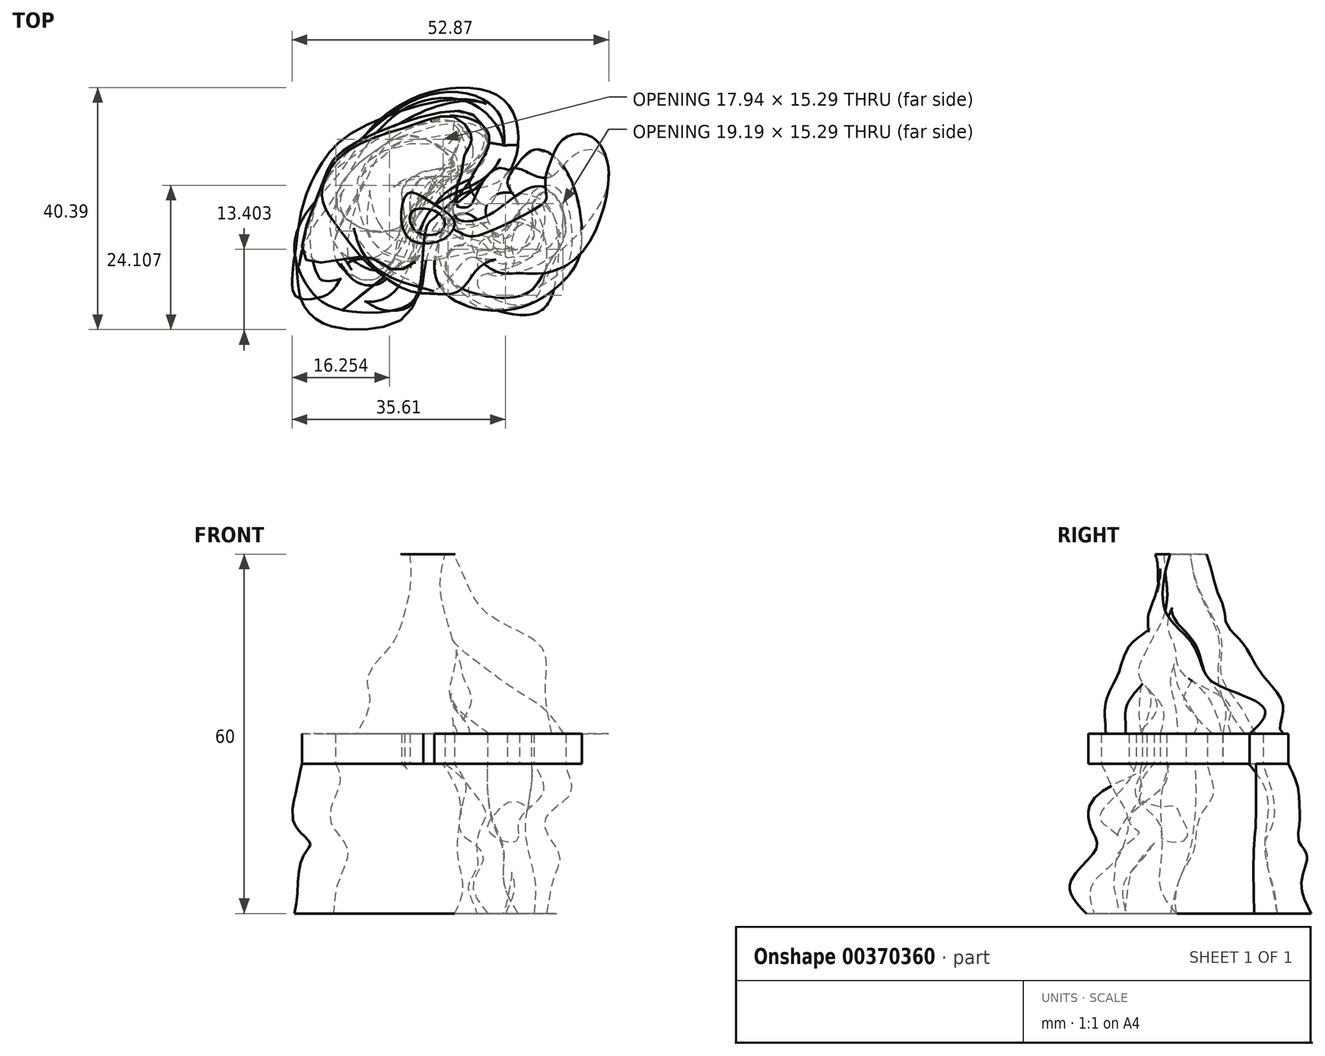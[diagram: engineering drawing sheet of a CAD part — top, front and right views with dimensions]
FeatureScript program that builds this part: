
annotation { "Feature Type Name" : "Feature", "Feature Type Description" : "" }
export const myFeature = defineFeature(function(context is Context, id is Id, definition is map)
    precondition{}
    {
        {
            var Q0;
            Q0=qCreatedBy(makeId("Top.planeOp"),FACE);
            cPlane(context, id + "F0", {"entities" : qUnion([Q0]), "cplaneType" : CPlaneType.OFFSET, "offset" : 5 * mm, "width" : 152.4 * mm, "height" : 152.4 * mm});
        }
        {
            var Q0;
            Q0=qCreatedBy(id+"F0.planeOp",FACE);
            var sketch = newSketch(context, id + "F1", { "sketchPlane" : qUnion([Q0])});
            skFitSpline(sketch, "E0", {"points": [v(10.66, 15.7) * mm, v(7.94, 23.44) * mm, v(-3.49, 24.6) * mm, v(-13.56, 18.8) * mm, v(-19.18, 11.04) * mm, v(-24.6, 4.46) * mm, v(-26.73, -1.55) * mm, v(-25, -7.17) * mm, v(-20.34, -11.43) * mm, v(-8.91, -11.62) * mm, v(-5.81, -7.94) * mm, v(-4.65, 1.94) * mm, v(-3.1, 3.68) * mm, v(1.55, 7.56) * mm, v(7.56, 9.69) * mm, v(10.66, 15.7) * mm]});
            skSolve(sketch);
        }
        {
            var Q0;
            Q0=qCreatedBy(id+"F0.planeOp",FACE);
            var sketch = newSketch(context, id + "F2", { "sketchPlane" : qUnion([Q0])});
            skFitSpline(sketch, "E1", {"points": [v(0, 2.71) * mm, v(-2.71, -1.94) * mm, v(1.74, -9.3) * mm, v(12.98, -12.6) * mm, v(16.66, -8.33) * mm, v(16.66, 3.68) * mm, v(13.95, 6.78) * mm, v(10.85, 7.56) * mm, v(6.97, 7.36) * mm, v(5.23, 4.84) * mm, v(6, 1.94) * mm, v(6.4, -1.74) * mm, v(4.84, -2.71) * mm, v(3.68, -2.71) * mm, v(2.9, 0) * mm, v(3.1, 2.71) * mm, v(0, 2.71) * mm]});
            skSolve(sketch);
        }
        {
            var Q0;
            Q0=qCreatedBy(id+"F0.planeOp",FACE);
            var sketch = newSketch(context, id + "F3", { "sketchPlane" : qUnion([Q0])});
            skFitSpline(sketch, "E2", {"points": [v(0, 19.57) * mm, v(-10.46, 16.66) * mm, v(-15.7, 7.94) * mm, v(-20.15, -2.32) * mm, v(-15.5, -6.78) * mm, v(-11.82, -5.81) * mm, v(-8.72, 0) * mm, v(-4.26, 8.14) * mm, v(2.13, 11.62) * mm, v(5.62, 17.05) * mm, v(0, 19.57) * mm]});
            skSolve(sketch);
        }
        {
            var Q0;
            Q0=qCreatedBy(id+"F0.planeOp",FACE);
            var sketch = newSketch(context, id + "F4", { "sketchPlane" : qUnion([Q0])});
            skFitSpline(sketch, "E3", {"points": [v(13.37, 1.74) * mm, v(9.5, 2.71) * mm, v(8.14, 0) * mm, v(8.33, -5.23) * mm, v(4.84, -6) * mm, v(3.87, -7.75) * mm, v(8.33, -10.66) * mm, v(12.98, -10.46) * mm, v(15.11, -6) * mm, v(15.11, 0) * mm, v(13.37, 1.74) * mm]});
            skSolve(sketch);
        }
        {
            var Q0;
            Q0=qCreatedBy(id+"F0.planeOp",FACE);
            cPlane(context, id + "F5", {"entities" : qUnion([Q0]), "cplaneType" : CPlaneType.OFFSET, "offset" : 5 * mm, "width" : 152.4 * mm, "height" : 152.4 * mm});
        }
        {
            var Q0;
            Q0=qCreatedBy(id+"F5.planeOp",FACE);
            var sketch = newSketch(context, id + "F6", { "sketchPlane" : qUnion([Q0])});
            skFitSpline(sketch, "E4", {"points": [v(3.1, 22.47) * mm, v(-6.78, 22.47) * mm, v(-14.14, 16.27) * mm, v(-20.15, 6.97) * mm, v(-24.6, 0) * mm, v(-25.96, -8.72) * mm, v(-21.31, -14.34) * mm, v(-8.91, -13.17) * mm, v(-6.78, -6.2) * mm, v(-4.07, 4.46) * mm, v(3.68, 9.3) * mm, v(8.33, 15.3) * mm, v(3.1, 22.47) * mm]});
            skSolve(sketch);
        }
        {
            var Q0;
            Q0=qCreatedBy(id+"F5.planeOp",FACE);
            var sketch = newSketch(context, id + "F7", { "sketchPlane" : qUnion([Q0])});
            skFitSpline(sketch, "E5", {"points": [v(1.74, 0) * mm, v(4.65, -1.74) * mm, v(8.91, 1.94) * mm, v(8.72, 9.3) * mm, v(12.6, 10.85) * mm, v(18.6, 9.5) * mm, v(20.54, 4.84) * mm, v(19.37, 0) * mm, v(16.47, -7.36) * mm, v(13.95, -9.88) * mm, v(6.4, -13.17) * mm, v(2.9, -12.6) * mm, v(0, -11.04) * mm, v(-1.94, -4.65) * mm, v(0, -1.74) * mm, v(1.74, 0) * mm]});
            skSolve(sketch);
        }
        {
            var Q0;
            Q0=qCreatedBy(id+"F5.planeOp",FACE);
            var sketch = newSketch(context, id + "F8", { "sketchPlane" : qUnion([Q0])});
            skFitSpline(sketch, "E6", {"points": [v(-1.95, 18.75) * mm, v(-12.28, 15.24) * mm, v(-14.78, 10.42) * mm, v(-18.5, 3.1) * mm, v(-19.3, -2.81) * mm, v(-16.29, -7.23) * mm, v(-12.38, -7.43) * mm, v(-10.17, -4.72) * mm, v(-8.97, 1.8) * mm, v(-4.46, 7.41) * mm, v(2.56, 12.43) * mm, v(2.56, 16.84) * mm, v(-1.95, 18.75) * mm]});
            skSolve(sketch);
        }
        {
            var Q0;
            Q0=qCreatedBy(id+"F5.planeOp",FACE);
            var sketch = newSketch(context, id + "F9", { "sketchPlane" : qUnion([Q0])});
            skFitSpline(sketch, "E7", {"points": [v(13.5, 3) * mm, v(10.59, 2) * mm, v(9.38, -0.9) * mm, v(9.99, -4.12) * mm, v(6.88, -6.02) * mm, v(4.47, -5.32) * mm, v(2.87, -5.82) * mm, v(2.46, -7.73) * mm, v(3.17, -10.84) * mm, v(9.58, -10.23) * mm, v(15.71, -5.86) * mm, v(15.71, 1.14) * mm, v(13.5, 3) * mm]});
            skSolve(sketch);
        }
        {
            var Q0;
            Q0=qCreatedBy(id+"F5.planeOp",FACE);
            cPlane(context, id + "F10", {"entities" : qUnion([Q0]), "cplaneType" : CPlaneType.OFFSET, "offset" : 5 * mm, "width" : 152.4 * mm, "height" : 152.4 * mm});
        }
        {
            var Q0;
            Q0=qCreatedBy(id+"F10.planeOp",FACE);
            var sketch = newSketch(context, id + "F11", { "sketchPlane" : qUnion([Q0])});
            skFitSpline(sketch, "E8", {"points": [v(-8.91, 21.9) * mm, v(2.9, 24.02) * mm, v(7.75, 19.95) * mm, v(7.17, 12.6) * mm, v(0, 5.62) * mm, v(-3.1, 2.32) * mm, v(-6.97, -3.49) * mm, v(-10.46, -9.5) * mm, v(-18.21, -11.04) * mm, v(-24.4, -7.17) * mm, v(-24.02, 2.9) * mm, v(-21.9, 8.91) * mm, v(-19.57, 12.2) * mm, v(-8.91, 21.9) * mm]});
            skSolve(sketch);
        }
        {
            var Q0;
            Q0=qCreatedBy(id+"F10.planeOp",FACE);
            var sketch = newSketch(context, id + "F12", { "sketchPlane" : qUnion([Q0])});
            skFitSpline(sketch, "E9", {"points": [v(0, -2.13) * mm, v(1.74, 2.13) * mm, v(3.87, 2.52) * mm, v(7.36, 2.13) * mm, v(9.88, 5.81) * mm, v(12.98, 7.56) * mm, v(16.85, 6.97) * mm, v(18.21, 3.1) * mm, v(18.4, -1.55) * mm, v(16.27, -4.84) * mm, v(12.2, -6.97) * mm, v(8.91, -7.75) * mm, v(4.26, -8.14) * mm, v(1.55, -5.62) * mm, v(0, -2.13) * mm]});
            skSolve(sketch);
        }
        {
            var Q0;
            Q0=qCreatedBy(id+"F10.planeOp",FACE);
            var sketch = newSketch(context, id + "F13", { "sketchPlane" : qUnion([Q0])});
            skFitSpline(sketch, "E10", {"points": [v(14.7, 5.4) * mm, v(11.29, 4) * mm, v(10.09, 2.3) * mm, v(6.68, -2.41) * mm, v(4.17, -2.31) * mm, v(3.87, -4.02) * mm, v(6.07, -6.32) * mm, v(13.6, -5.72) * mm, v(16.9, -2.41) * mm, v(17.4, 1.7) * mm, v(14.7, 5.4) * mm]});
            skSolve(sketch);
        }
        {
            var Q0;
            Q0=qCreatedBy(id+"F10.planeOp",FACE);
            var sketch = newSketch(context, id + "F14", { "sketchPlane" : qUnion([Q0])});
            skFitSpline(sketch, "E11", {"points": [v(-0.95, 17.44) * mm, v(-13.38, 14.13) * mm, v(-15.29, 9.52) * mm, v(-17.8, -1.1) * mm, v(-15.49, -6.93) * mm, v(-8.77, -3.01) * mm, v(-5.46, 7.72) * mm, v(0, 11.53) * mm, v(3.87, 13.93) * mm, v(4.57, 17.24) * mm, v(-0.95, 17.44) * mm]});
            skSolve(sketch);
        }
        {
            var Q0;
            Q0=qCreatedBy(id+"F10.planeOp",FACE);
            cPlane(context, id + "F15", {"entities" : qUnion([Q0]), "cplaneType" : CPlaneType.OFFSET, "offset" : 5 * mm, "width" : 152.4 * mm, "height" : 152.4 * mm});
        }
        {
            var Q0;
            Q0=qCreatedBy(id+"F15.planeOp",FACE);
            var sketch = newSketch(context, id + "F16", { "sketchPlane" : qUnion([Q0])});
            skFitSpline(sketch, "E12", {"points": [v(-17.05, 13.75) * mm, v(-5.81, 21.31) * mm, v(5.62, 21.9) * mm, v(4.84, 11.82) * mm, v(0, 8.72) * mm, v(-4.65, 3.68) * mm, v(-7.17, -3.87) * mm, v(-8.14, -10.07) * mm, v(-10.07, -11.62) * mm, v(-13.17, -11.43) * mm, v(-15.3, -8.91) * mm, v(-15.89, -6.78) * mm, v(-18.6, -6.4) * mm, v(-20.54, -8.52) * mm, v(-22.09, -9.3) * mm, v(-25.18, -9.5) * mm, v(-26.54, -8.72) * mm, v(-26.35, -2.71) * mm, v(-24.22, 7.36) * mm, v(-17.05, 13.75) * mm]});
            skSolve(sketch);
        }
        {
            var Q0;
            Q0=qCreatedBy(id+"F15.planeOp",FACE);
            var sketch = newSketch(context, id + "F17", { "sketchPlane" : qUnion([Q0])});
            skFitSpline(sketch, "E13", {"points": [v(0, 18.6) * mm, v(-12.7, 13.89) * mm, v(-15.9, 9.73) * mm, v(-20.33, 2.38) * mm, v(-19.78, -1.22) * mm, v(-16.31, -4) * mm, v(-11.74, -4.68) * mm, v(-4.67, 7.23) * mm, v(0, 14.02) * mm, v(0, 18.6) * mm]});
            skSolve(sketch);
        }
        {
            var Q0;
            Q0=qCreatedBy(id+"F15.planeOp",FACE);
            var sketch = newSketch(context, id + "F18", { "sketchPlane" : qUnion([Q0])});
            skFitSpline(sketch, "E14", {"points": [v(14.6, 5.85) * mm, v(11.4, 5.3) * mm, v(9.32, 1.83) * mm, v(5.72, 0) * mm, v(4.75, -3.02) * mm, v(6.7, -5.24) * mm, v(11.54, -3.85) * mm, v(13.9, -1.5) * mm, v(14.6, 5.85) * mm]});
            skSolve(sketch);
        }
        {
            var Q0;
            Q0=qCreatedBy(id+"F15.planeOp",FACE);
            cPlane(context, id + "F19", {"entities" : qUnion([Q0]), "cplaneType" : CPlaneType.OFFSET, "offset" : 5 * mm, "width" : 152.4 * mm, "height" : 152.4 * mm});
        }
        {
            var Q0;
            Q0=qCreatedBy(id+"F19.planeOp",FACE);
            var sketch = newSketch(context, id + "F20", { "sketchPlane" : qUnion([Q0])});
            skFitSpline(sketch, "E15", {"points": [v(0, -2.9) * mm, v(2.13, 2.32) * mm, v(6.97, -1.74) * mm, v(10.27, -2.71) * mm, v(13.17, 2.32) * mm, v(11.62, 3.49) * mm, v(8.78, 5.55) * mm, v(7.73, 7.13) * mm, v(10.2, 11.79) * mm, v(15.4, 12.24) * mm, v(18.99, 10.07) * mm, v(21.31, 3.87) * mm, v(21.5, -4.26) * mm, v(17.24, -7.75) * mm, v(10.46, -8.72) * mm, v(3.68, -8.72) * mm, v(0, -7.56) * mm, v(0, -2.9) * mm]});
            skSolve(sketch);
        }
        {
            var Q0;
            Q0=qCreatedBy(id+"F19.planeOp",FACE);
            var sketch = newSketch(context, id + "F21", { "sketchPlane" : qUnion([Q0])});
            skFitSpline(sketch, "E16", {"points": [v(-25.96, -5.81) * mm, v(-22.09, -6.97) * mm, v(-18.6, -4.84) * mm, v(-16.47, -3.3) * mm, v(-13.37, -3.87) * mm, v(-12.79, -6.4) * mm, v(-11.82, -9.3) * mm, v(-7.56, -10.07) * mm, v(-5.42, -7.94) * mm, v(-4.65, -3.3) * mm, v(0, 6) * mm, v(1.55, 8.33) * mm, v(5.62, 15.89) * mm, v(2.32, 22.28) * mm, v(-4.26, 22.67) * mm, v(-15.5, 18.21) * mm, v(-22.09, 12.79) * mm, v(-25.57, 2.71) * mm, v(-25.96, -5.81) * mm]});
            skSolve(sketch);
        }
        {
            var Q0;
            Q0=qCreatedBy(id+"F19.planeOp",FACE);
            var sketch = newSketch(context, id + "F22", { "sketchPlane" : qUnion([Q0])});
            skFitSpline(sketch, "E17", {"points": [v(0, 18.32) * mm, v(-8.7, 16.52) * mm, v(-12.3, 13.47) * mm, v(-17.28, 9.87) * mm, v(-19.5, 3.08) * mm, v(-14.37, 0) * mm, v(-8.7, 0) * mm, v(-3.15, 9.17) * mm, v(1.56, 13.05) * mm, v(0, 18.32) * mm]});
            skSolve(sketch);
        }
        {
            var Q0;
            Q0=qCreatedBy(id+"F19.planeOp",FACE);
            var sketch = newSketch(context, id + "F23", { "sketchPlane" : qUnion([Q0])});
            skFitSpline(sketch, "E18", {"points": [v(12.65, 7.1) * mm, v(13.9, 3.9) * mm, v(14.73, 0) * mm, v(13.2, -2.6) * mm, v(7.8, -4.13) * mm, v(5.44, -3.44) * mm, v(3.78, -4.13) * mm, v(3.92, -6.62) * mm, v(16.8, -5.52) * mm, v(19.44, 0) * mm, v(16.4, 8.76) * mm, v(12.65, 7.1) * mm]});
            skSolve(sketch);
        }
        {
            var Q0;
            Q0=qCreatedBy(id+"F19.planeOp",FACE);
            cPlane(context, id + "F24", {"entities" : qUnion([Q0]), "cplaneType" : CPlaneType.OFFSET, "offset" : 5 * mm, "width" : 152.4 * mm, "height" : 152.4 * mm});
        }
        {
            var Q0;
            Q0=qCreatedBy(id+"F24.planeOp",FACE);
            var sketch = newSketch(context, id + "F25", { "sketchPlane" : qUnion([Q0])});
            skFitSpline(sketch, "E19", {"points": [v(-25, -3.3) * mm, v(-16.66, -3.1) * mm, v(-12.79, -3.68) * mm, v(-9.5, -5.23) * mm, v(-5.62, -2.71) * mm, v(-5.42, 0) * mm, v(-6.97, 3.3) * mm, v(-7.36, 6.78) * mm, v(-6, 9.69) * mm, v(-3.68, 10.46) * mm, v(0, 10.46) * mm, v(5.04, 13.17) * mm, v(4.07, 19.95) * mm, v(-2.32, 21.12) * mm, v(-15.3, 16.66) * mm, v(-20.34, 12.98) * mm, v(-22.67, 7.56) * mm, v(-25, -3.3) * mm]});
            skSolve(sketch);
        }
        {
            var Q0;
            Q0=qCreatedBy(id+"F24.planeOp",FACE);
            var sketch = newSketch(context, id + "F26", { "sketchPlane" : qUnion([Q0])});
            skFitSpline(sketch, "E20", {"points": [v(2.9, 3.87) * mm, v(0, 3.87) * mm, v(-2.09, 1.21) * mm, v(-3.3, -5.42) * mm, v(0, -10.27) * mm, v(10.46, -11.62) * mm, v(19.18, -6) * mm, v(21.31, 0) * mm, v(18.4, 11.82) * mm, v(13.56, 14.92) * mm, v(10.66, 12.61) * mm, v(8.86, 9.23) * mm, v(10.46, 6.4) * mm, v(10.46, 2.13) * mm, v(8.14, 0) * mm, v(2.9, 3.87) * mm]});
            skSolve(sketch);
        }
        {
            var Q0;
            Q0=qCreatedBy(id+"F24.planeOp",FACE);
            var sketch = newSketch(context, id + "F27", { "sketchPlane" : qUnion([Q0])});
            skFitSpline(sketch, "E21", {"points": [v(-6.2, 17.07) * mm, v(-12.7, 15) * mm, v(-17.56, 10.98) * mm, v(-19.64, 5.3) * mm, v(-14.1, 1.28) * mm, v(-11.18, 1.28) * mm, v(-8.41, 2.8) * mm, v(-8.7, 8.2) * mm, v(-3.84, 11.53) * mm, v(0, 12.36) * mm, v(-6.2, 17.07) * mm]});
            skSolve(sketch);
        }
        {
            var Q0;
            Q0=qCreatedBy(id+"F24.planeOp",FACE);
            var sketch = newSketch(context, id + "F28", { "sketchPlane" : qUnion([Q0])});
            skFitSpline(sketch, "E22", {"points": [v(15.98, 7.79) * mm, v(12.93, 5.57) * mm, v(13.2, 0) * mm, v(10.02, -1.91) * mm, v(5.72, -2.05) * mm, v(0, -1.22) * mm, v(-1.48, -5.24) * mm, v(2.12, -8.7) * mm, v(12.1, -9.12) * mm, v(15.84, -4) * mm, v(18.6, 1.28) * mm, v(15.98, 7.79) * mm]});
            skSolve(sketch);
        }
        {
            var Q0;
            Q0=qCreatedBy(id+"F24.planeOp",FACE);
            cPlane(context, id + "F29", {"entities" : qUnion([Q0]), "cplaneType" : CPlaneType.OFFSET, "offset" : 5 * mm, "width" : 152.4 * mm, "height" : 152.4 * mm});
        }
        {
            var Q0;
            Q0=qCreatedBy(id+"F29.planeOp",FACE);
            var sketch = newSketch(context, id + "F30", { "sketchPlane" : qUnion([Q0])});
            skFitSpline(sketch, "E23", {"points": [v(16.27, 10.46) * mm, v(20.54, 14.34) * mm, v(24.8, 14.14) * mm, v(25.57, 8.91) * mm, v(23.44, 4.46) * mm, v(17.24, -2.32) * mm, v(7.36, -5.62) * mm, v(3.1, -3.1) * mm, v(0, -5.62) * mm, v(-5.23, -9.1) * mm, v(-14.14, -4.46) * mm, v(-18.02, 0) * mm, v(-21.31, 4.65) * mm, v(-22.09, 7.94) * mm, v(-18.02, 14.53) * mm, v(-3.49, 19.76) * mm, v(0, 20.54) * mm, v(5.23, 18.4) * mm, v(5.04, 13.95) * mm, v(2.52, 9.3) * mm, v(5.42, 5.62) * mm, v(8.14, 9.88) * mm, v(9.88, 11.82) * mm, v(13.17, 10.66) * mm, v(16.27, 10.46) * mm]});
            skSolve(sketch);
        }
        {
            var Q0;
            Q0=qCreatedBy(id+"F29.planeOp",FACE);
            var sketch = newSketch(context, id + "F31", { "sketchPlane" : qUnion([Q0])});
            skFitSpline(sketch, "E24", {"points": [v(0, 14.16) * mm, v(-13.54, 13.75) * mm, v(-16.17, 6.13) * mm, v(-11.46, -2.74) * mm, v(-1.48, -2.6) * mm, v(3.78, 0) * mm, v(7.1, -2.74) * mm, v(17.36, 0) * mm, v(16.95, 7.1) * mm, v(12.93, 8.62) * mm, v(5.03, 3.63) * mm, v(0, 4.05) * mm, v(0, 14.16) * mm]});
            skSolve(sketch);
        }
        {
            var Q0;
            Q0=qCreatedBy(id+"F29.planeOp",FACE);
            cPlane(context, id + "F32", {"entities" : qUnion([Q0]), "cplaneType" : CPlaneType.OFFSET, "offset" : 5 * mm, "width" : 152.4 * mm, "height" : 152.4 * mm});
        }
        {
            var Q0;
            Q0=qCreatedBy(id+"F32.planeOp",FACE);
            var sketch = newSketch(context, id + "F33", { "sketchPlane" : qUnion([Q0])});
            skFitSpline(sketch, "E25", {"points": [v(-6.97, 17.82) * mm, v(-15.89, 14.34) * mm, v(-18.4, 7.36) * mm, v(-17.63, 0) * mm, v(-10.66, -5.42) * mm, v(-10.07, -5.62) * mm, v(-1.94, -9.1) * mm, v(1.94, -7.56) * mm, v(4.26, -4.65) * mm, v(8.14, -3.49) * mm, v(13.37, -5.42) * mm, v(19.76, -3.3) * mm, v(23.44, 2.9) * mm, v(24.4, 10.07) * mm, v(21.7, 16.08) * mm, v(18.02, 16.08) * mm, v(15.7, 11.82) * mm, v(14.14, 8.91) * mm, v(11.82, 8.72) * mm, v(10.07, 9.69) * mm, v(6.78, 11.43) * mm, v(3.68, 6.78) * mm, v(3.3, 5.04) * mm, v(0, 4.26) * mm, v(0, 7.56) * mm, v(0, 14.53) * mm, v(2.71, 16.66) * mm, v(0, 20.34) * mm, v(-6.97, 17.82) * mm]});
            skSolve(sketch);
        }
        {
            var Q0;
            Q0=qCreatedBy(id+"F32.planeOp",FACE);
            var sketch = newSketch(context, id + "F34", { "sketchPlane" : qUnion([Q0])});
            skFitSpline(sketch, "E26", {"points": [v(-2.18, 10.14) * mm, v(-12.3, 12.64) * mm, v(-14.1, 7.51) * mm, v(-10.08, 0) * mm, v(3.92, 0) * mm, v(11.13, -1.36) * mm, v(13.76, 3.9) * mm, v(10.16, 4.46) * mm, v(4.9, 2.94) * mm, v(0, 3.08) * mm, v(-2.18, 10.14) * mm]});
            skSolve(sketch);
        }
        {
            var Q0;
            Q0=qCreatedBy(id+"F32.planeOp",FACE);
            cPlane(context, id + "F35", {"entities" : qUnion([Q0]), "cplaneType" : CPlaneType.OFFSET, "offset" : 5 * mm, "width" : 152.4 * mm, "height" : 152.4 * mm});
        }
        {
            var Q0;
            Q0=qCreatedBy(id+"F35.planeOp",FACE);
            var sketch = newSketch(context, id + "F36", { "sketchPlane" : qUnion([Q0])});
            skFitSpline(sketch, "E27", {"points": [v(-15.11, 12.79) * mm, v(-10.27, 15.11) * mm, v(-2.32, 16.66) * mm, v(0, 16.66) * mm, v(1.36, 12.01) * mm, v(0, 8.33) * mm, v(0, 5.81) * mm, v(1.74, 5.04) * mm, v(4.84, 3.87) * mm, v(10.07, 4.84) * mm, v(13.75, 7.36) * mm, v(18.8, 6) * mm, v(18.21, 0) * mm, v(14.72, -2.32) * mm, v(8.72, -2.52) * mm, v(6.2, -1.94) * mm, v(2.32, -3.1) * mm, v(0, -5.42) * mm, v(-8.91, -6.78) * mm, v(-16.27, 0) * mm, v(-15.11, 12.79) * mm]});
            skSolve(sketch);
        }
        {
            var Q0;
            Q0=qCreatedBy(id+"F35.planeOp",FACE);
            var sketch = newSketch(context, id + "F37", { "sketchPlane" : qUnion([Q0])});
            skFitSpline(sketch, "E28", {"points": [v(-4.4, 10) * mm, v(-12.3, 7.51) * mm, v(-13.82, 0) * mm, v(-8.27, -3.16) * mm, v(-1.48, -3.16) * mm, v(3.92, 0) * mm, v(6.41, 1.28) * mm, v(4.9, 2.52) * mm, v(0, 1.97) * mm, v(-2.32, 7.23) * mm, v(-4.4, 10) * mm]});
            skSolve(sketch);
        }
        {
            var Q0;
            Q0=qCreatedBy(id+"F35.planeOp",FACE);
            cPlane(context, id + "F38", {"entities" : qUnion([Q0]), "cplaneType" : CPlaneType.OFFSET, "offset" : 5 * mm, "width" : 152.4 * mm, "height" : 152.4 * mm});
        }
        {
            var Q0;
            Q0=qCreatedBy(id+"F38.planeOp",FACE);
            var sketch = newSketch(context, id + "F39", { "sketchPlane" : qUnion([Q0])});
            skFitSpline(sketch, "E29", {"points": [v(-3.49, 13.56) * mm, v(-12.01, 11.82) * mm, v(-12.98, 5.81) * mm, v(-9.1, -2.52) * mm, v(-4.26, -4.84) * mm, v(0, -2.52) * mm, v(10.07, -1.74) * mm, v(16.47, 1.74) * mm, v(12.79, 5.81) * mm, v(6.4, 2.71) * mm, v(1.36, 3.3) * mm, v(0, 9.1) * mm, v(-3.49, 13.56) * mm]});
            skSolve(sketch);
        }
        {
            var Q0;
            Q0=qCreatedBy(id+"F38.planeOp",FACE);
            var sketch = newSketch(context, id + "F40", { "sketchPlane" : qUnion([Q0])});
            skFitSpline(sketch, "E30", {"points": [v(-1.76, 8.76) * mm, v(-8.55, 9.73) * mm, v(-10.21, 4.32) * mm, v(-5.36, -1.64) * mm, v(0, 0) * mm, v(0, 2.25) * mm, v(-1.76, 8.76) * mm]});
            skSolve(sketch);
        }
        {
            var Q0;
            Q0=qCreatedBy(id+"F38.planeOp",FACE);
            cPlane(context, id + "F41", {"entities" : qUnion([Q0]), "cplaneType" : CPlaneType.OFFSET, "offset" : 5 * mm, "width" : 152.4 * mm, "height" : 152.4 * mm});
        }
        {
            var Q0;
            Q0=qCreatedBy(id+"F41.planeOp",FACE);
            var sketch = newSketch(context, id + "F42", { "sketchPlane" : qUnion([Q0])});
            skFitSpline(sketch, "E31", {"points": [v(-2.32, 9.5) * mm, v(-9.88, 10.07) * mm, v(-10.07, 3.49) * mm, v(-6.78, 0) * mm, v(0, -1.94) * mm, v(5.62, 0) * mm, v(4.46, 1.94) * mm, v(0, 1.55) * mm, v(0, 2.13) * mm, v(0, 6.2) * mm, v(-2.32, 9.5) * mm]});
            skSolve(sketch);
        }
        {
            var Q0;
            Q0=qCreatedBy(id+"F41.planeOp",FACE);
            var sketch = newSketch(context, id + "F43", { "sketchPlane" : qUnion([Q0])});
            skFitSpline(sketch, "E32", {"points": [v(-3.14, 7.61) * mm, v(-7.34, 7.94) * mm, v(-8.33, 4.32) * mm, v(-7.1, 2.17) * mm, v(-3.22, 0.7) * mm, v(-1.66, 2.26) * mm, v(-3.14, 7.61) * mm]});
            skSolve(sketch);
        }
        {
            var Q0;
            Q0=qCreatedBy(id+"F41.planeOp",FACE);
            cPlane(context, id + "F44", {"entities" : qUnion([Q0]), "cplaneType" : CPlaneType.OFFSET, "offset" : 5 * mm, "width" : 152.4 * mm, "height" : 152.4 * mm});
        }
        {
            var Q0;
            Q0=qCreatedBy(id+"F44.planeOp",FACE);
            var sketch = newSketch(context, id + "F45", { "sketchPlane" : qUnion([Q0])});
            skFitSpline(sketch, "E33", {"points": [v(-1.74, 5.23) * mm, v(-5.04, 8.72) * mm, v(-9.88, 7.56) * mm, v(-6.2, 0) * mm, v(-2.52, 0) * mm, v(2.13, 0) * mm, v(0, 3.87) * mm, v(-1.74, 5.23) * mm]});
            skSolve(sketch);
        }
        {
            var Q0;
            Q0=qCreatedBy(id+"F44.planeOp",FACE);
            var sketch = newSketch(context, id + "F46", { "sketchPlane" : qUnion([Q0])});
            skFitSpline(sketch, "E34", {"points": [v(-2.81, 4.23) * mm, v(-5.78, 6.13) * mm, v(-7.34, 3.99) * mm, v(-5.28, 1.35) * mm, v(-2.73, 1.51) * mm, v(-2.81, 4.23) * mm]});
            skSolve(sketch);
        }
        {
            var Q0;
            Q0=qCreatedBy(id+"F44.planeOp",FACE);
            cPlane(context, id + "F47", {"entities" : qUnion([Q0]), "cplaneType" : CPlaneType.OFFSET, "offset" : 5 * mm, "width" : 152.4 * mm, "height" : 152.4 * mm});
        }
        {
            var Q0;
            Q0=qCreatedBy(id+"F47.planeOp",FACE);
            var sketch = newSketch(context, id + "F48", { "sketchPlane" : qUnion([Q0])});
            skFitSpline(sketch, "E35", {"points": [v(-3.49, 5.81) * mm, v(-7.36, 7.75) * mm, v(-8.72, 5.62) * mm, v(-7.56, 0) * mm, v(-1.74, 0) * mm, v(0, 2.9) * mm, v(-3.49, 5.81) * mm]});
            skSolve(sketch);
        }
        {
            var Q0;
            Q0=qCreatedBy(id+"F47.planeOp",FACE);
            var sketch = newSketch(context, id + "F49", { "sketchPlane" : qUnion([Q0])});
            skFitSpline(sketch, "E36", {"points": [v(-4.87, 5.06) * mm, v(-7.26, 4.32) * mm, v(-7.18, 2.26) * mm, v(-5.53, 0.77) * mm, v(-2.32, 1.18) * mm, v(-1.74, 3.33) * mm, v(-4.87, 5.06) * mm]});
            skSolve(sketch);
        }
        {
            var Q0;
            Q0=makeQuery(id+"F30.imprint","IMPRINT",FACE,{"disambiguationData":[TD([[makeQuery(id+"F30.imprint","IMPRINT",EDGE,{"derivedFrom":sQuery(id+"F30.wireOp",EDGE,"E23")}),-1.0]])]});
            var Q1;
            Q1=makeQuery(id+"F33.imprint","IMPRINT",FACE,{"disambiguationData":[TD([[makeQuery(id+"F33.imprint","IMPRINT",EDGE,{"derivedFrom":sQuery(id+"F33.wireOp",EDGE,"E25")}),1.0]])]});
            var Q2;
            Q2=makeQuery(id+"F36.imprint","IMPRINT",FACE,{"disambiguationData":[TD([[makeQuery(id+"F36.imprint","IMPRINT",EDGE,{"derivedFrom":sQuery(id+"F36.wireOp",EDGE,"E27")}),-1.0]])]});
            var Q3;
            Q3=makeQuery(id+"F39.imprint","IMPRINT",FACE,{"disambiguationData":[TD([[makeQuery(id+"F39.imprint","IMPRINT",EDGE,{"derivedFrom":sQuery(id+"F39.wireOp",EDGE,"E29")}),1.0]])]});
            var Q4;
            Q4=makeQuery(id+"F42.imprint","IMPRINT",FACE,{"disambiguationData":[TD([[makeQuery(id+"F42.imprint","IMPRINT",EDGE,{"derivedFrom":sQuery(id+"F42.wireOp",EDGE,"E31")}),1.0]])]});
            var Q5;
            Q5=makeQuery(id+"F45.imprint","IMPRINT",FACE,{"disambiguationData":[TD([[makeQuery(id+"F45.imprint","IMPRINT",EDGE,{"derivedFrom":sQuery(id+"F45.wireOp",EDGE,"E33")}),1.0]])]});
            var Q6;
            Q6=makeQuery(id+"F48.imprint","IMPRINT",FACE,{"disambiguationData":[TD([[makeQuery(id+"F48.imprint","IMPRINT",EDGE,{"derivedFrom":sQuery(id+"F48.wireOp",EDGE,"E35")}),1.0]])]});
            loft(context, id + "F50", {"sheetProfilesArray" : [{ "sheetProfileEntities" : qUnion([Q0]) }, { "sheetProfileEntities" : qUnion([Q1]) }, { "sheetProfileEntities" : qUnion([Q2]) }, { "sheetProfileEntities" : qUnion([Q3]) }, { "sheetProfileEntities" : qUnion([Q4]) }, { "sheetProfileEntities" : qUnion([Q5]) }, { "sheetProfileEntities" : qUnion([Q6]) }]});
        }
        {
            var Q1;
            Q1=qSketchRegion(id+"F31",true);
            var Q2;
            Q2=qSketchRegion(id+"F34",true);
            var Q3;
            Q3=qSketchRegion(id+"F37",true);
            var Q4;
            Q4=qSketchRegion(id+"F40",true);
            var Q5;
            Q5=qSketchRegion(id+"F43",true);
            var Q6;
            Q6=qSketchRegion(id+"F46",true);
            var Q7;
            Q7=qSketchRegion(id+"F49",true);
            loft(context, id + "F51", {"operationType" : NewBodyOperationType.REMOVE, "sheetProfilesArray" : [{ "sheetProfileEntities" : qUnion([Q1]) }, { "sheetProfileEntities" : qUnion([Q2]) }, { "sheetProfileEntities" : qUnion([Q3]) }, { "sheetProfileEntities" : qUnion([Q4]) }, { "sheetProfileEntities" : qUnion([Q5]) }, { "sheetProfileEntities" : qUnion([Q6]) }, { "sheetProfileEntities" : qUnion([Q7]) }]});
        }
        {
            var Q0;
            Q0=qSketchRegion(id+"F1",true);
            var Q1;
            Q1=qSketchRegion(id+"F6",true);
            var Q2;
            Q2=qSketchRegion(id+"F11",true);
            var Q3;
            Q3=qSketchRegion(id+"F16",true);
            var Q4;
            Q4=qSketchRegion(id+"F21",true);
            var Q5;
            Q5=qSketchRegion(id+"F25",true);
            loft(context, id + "F52", {"sheetProfilesArray" : [{ "sheetProfileEntities" : qUnion([Q0]) }, { "sheetProfileEntities" : qUnion([Q1]) }, { "sheetProfileEntities" : qUnion([Q2]) }, { "sheetProfileEntities" : qUnion([Q3]) }, { "sheetProfileEntities" : qUnion([Q4]) }, { "sheetProfileEntities" : qUnion([Q5]) }]});
        }
        {
            var Q1;
            Q1=qSketchRegion(id+"F3",true);
            var Q2;
            Q2=qSketchRegion(id+"F8",true);
            var Q3;
            Q3=qSketchRegion(id+"F14",true);
            var Q4;
            Q4=qSketchRegion(id+"F17",true);
            var Q5;
            Q5=qSketchRegion(id+"F22",true);
            var Q6;
            Q6=qSketchRegion(id+"F27",true);
            loft(context, id + "F53", {"operationType" : NewBodyOperationType.REMOVE, "sheetProfilesArray" : [{ "sheetProfileEntities" : qUnion([Q1]) }, { "sheetProfileEntities" : qUnion([Q2]) }, { "sheetProfileEntities" : qUnion([Q3]) }, { "sheetProfileEntities" : qUnion([Q4]) }, { "sheetProfileEntities" : qUnion([Q5]) }, { "sheetProfileEntities" : qUnion([Q6]) }]});
        }
        {
            var Q0;
            Q0=makeQuery(id+"F2.imprint","IMPRINT",FACE,{"disambiguationData":[TD([[makeQuery(id+"F2.imprint","IMPRINT",EDGE,{"derivedFrom":sQuery(id+"F2.wireOp",EDGE,"E1")}),1.0]])]});
            var Q1;
            Q1=makeQuery(id+"F7.imprint","IMPRINT",FACE,{"disambiguationData":[TD([[makeQuery(id+"F7.imprint","IMPRINT",EDGE,{"derivedFrom":sQuery(id+"F7.wireOp",EDGE,"E5")}),-1.0]])]});
            var Q2;
            Q2=makeQuery(id+"F12.imprint","IMPRINT",FACE,{"disambiguationData":[TD([[makeQuery(id+"F12.imprint","IMPRINT",EDGE,{"derivedFrom":sQuery(id+"F12.wireOp",EDGE,"E9")}),-1.0]])]});
            var Q3;
            Q3=makeQuery(id+"F20.imprint","IMPRINT",FACE,{"disambiguationData":[TD([[makeQuery(id+"F20.imprint","IMPRINT",EDGE,{"derivedFrom":sQuery(id+"F20.wireOp",EDGE,"E15")}),-1.0]])]});
            var Q4;
            Q4=makeQuery(id+"F26.imprint","IMPRINT",FACE,{"disambiguationData":[TD([[makeQuery(id+"F26.imprint","IMPRINT",EDGE,{"derivedFrom":sQuery(id+"F26.wireOp",EDGE,"E20")}),1.0]])]});
            loft(context, id + "F54", {"sheetProfilesArray" : [{ "sheetProfileEntities" : qUnion([Q0]) }, { "sheetProfileEntities" : qUnion([Q1]) }, { "sheetProfileEntities" : qUnion([Q2]) }, { "sheetProfileEntities" : qUnion([Q3]) }, { "sheetProfileEntities" : qUnion([Q4]) }]});
        }
        {
            var Q1;
            Q1=qSketchRegion(id+"F4",true);
            var Q2;
            Q2=qSketchRegion(id+"F9",true);
            var Q3;
            Q3=qSketchRegion(id+"F13",true);
            var Q4;
            Q4=qSketchRegion(id+"F18",true);
            var Q5;
            Q5=qSketchRegion(id+"F23",true);
            var Q6;
            Q6=qSketchRegion(id+"F28",true);
            loft(context, id + "F55", {"operationType" : NewBodyOperationType.REMOVE, "sheetProfilesArray" : [{ "sheetProfileEntities" : qUnion([Q1]) }, { "sheetProfileEntities" : qUnion([Q2]) }, { "sheetProfileEntities" : qUnion([Q3]) }, { "sheetProfileEntities" : qUnion([Q4]) }, { "sheetProfileEntities" : qUnion([Q5]) }, { "sheetProfileEntities" : qUnion([Q6]) }]});
        }
        {
            var Q0;
            Q0=makeQuery(id+"F52.opLoft","CAP_FACE",FACE,{"disambiguationData":[OSD([makeQuery(id+"F25.imprint","IMPRINT",FACE,{"disambiguationData":[TD([[makeQuery(id+"F25.imprint","IMPRINT",EDGE,{"derivedFrom":sQuery(id+"F25.wireOp",EDGE,"E19")}),1.0]])]})])],"isStart":true});
            extrude(context, id + "F56", {"entities" : qUnion([Q0]), "depth" : 5 * mm});
        }
        {
            var Q0;
            Q0=makeQuery(id+"F54.opLoft","CAP_FACE",FACE,{"disambiguationData":[OSD([makeQuery(id+"F26.imprint","IMPRINT",FACE,{"disambiguationData":[TD([[makeQuery(id+"F26.imprint","IMPRINT",EDGE,{"derivedFrom":sQuery(id+"F26.wireOp",EDGE,"E20")}),1.0]])]})])],"isStart":true});
            extrude(context, id + "F57", {"entities" : qUnion([Q0]), "depth" : 5 * mm});
        }
    });
